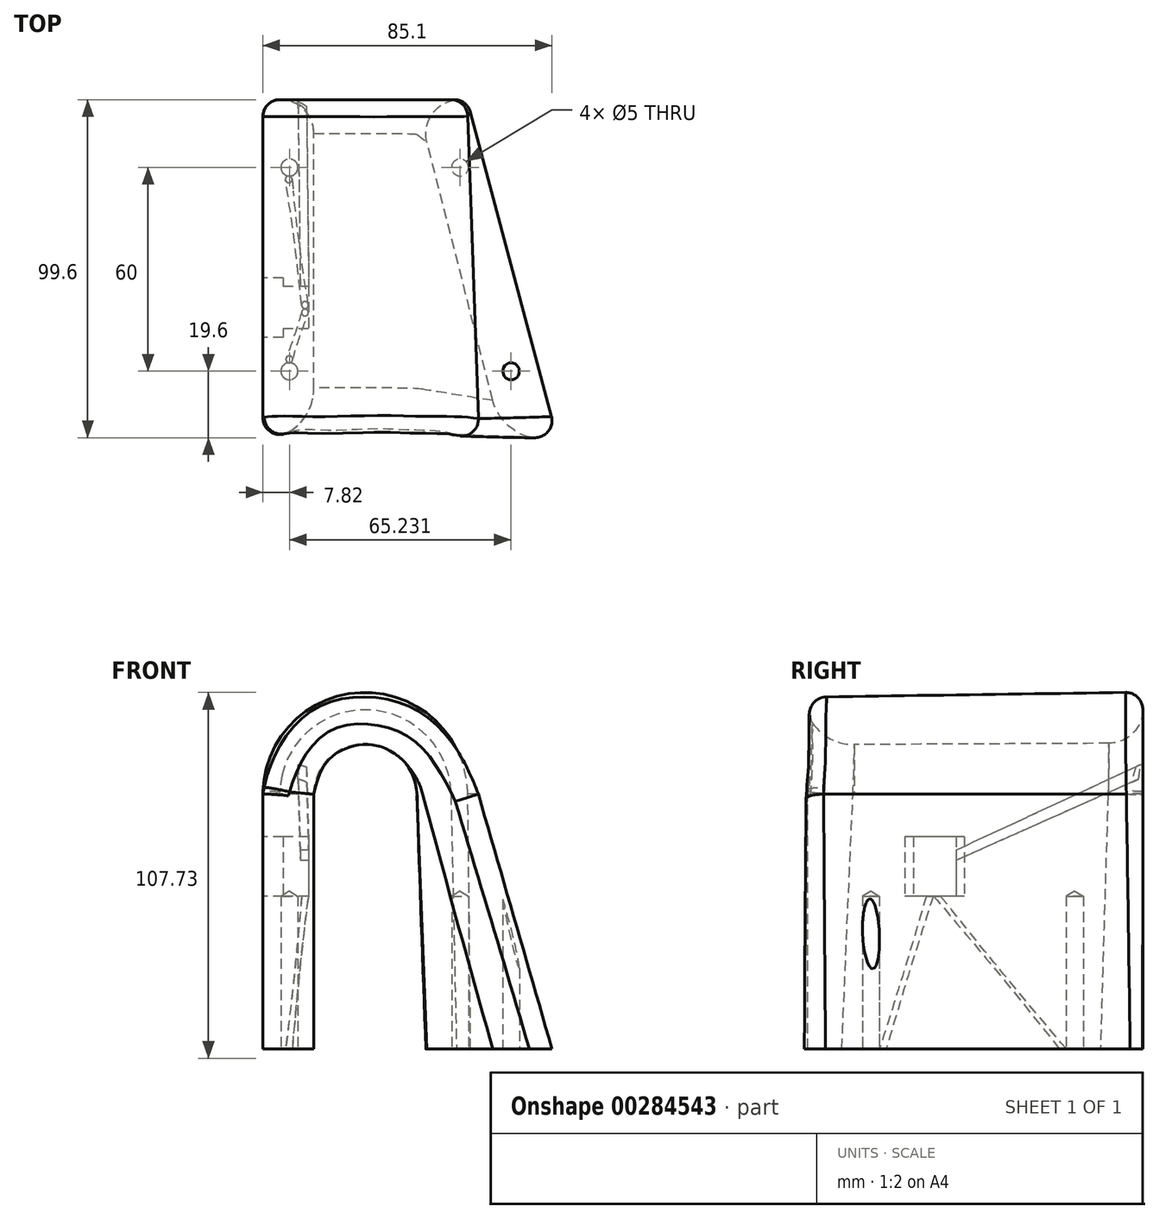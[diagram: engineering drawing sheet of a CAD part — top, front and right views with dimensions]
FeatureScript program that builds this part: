
annotation { "Feature Type Name" : "Feature", "Feature Type Description" : "" }
export const myFeature = defineFeature(function(context is Context, id is Id, definition is map)
    precondition{}
    {
        {
            var Q0;
            Q0=qCreatedBy(makeId("Top.planeOp"),FACE);
            var sketch = newSketch(context, id + "F0", { "sketchPlane" : qUnion([Q0])});
            skLineSegment(sketch, "E0.bottom", {"start": v(-34.5, 0) * mm, "end": v(-19.5, 0) * mm});
            skLineSegment(sketch, "E0.top", {"start": v(-34.5, 100) * mm, "end": v(-19.5, 100) * mm});
            skLineSegment(sketch, "E0.left", {"start": v(-34.5, 0) * mm, "end": v(-34.5, 100) * mm});
            skLineSegment(sketch, "E0.right", {"start": v(-19.5, 0) * mm, "end": v(-19.5, 100) * mm});
            skLineSegment(sketch, "E1", {"start": v(10.5, 100) * mm, "end": v(35.5, 0) * mm});
            skLineSegment(sketch, "E2", {"start": v(35.5, 0) * mm, "end": v(50.96, 0) * mm});
            skLineSegment(sketch, "E3", {"start": v(50.96, 0) * mm, "end": v(25.96, 100) * mm});
            skLineSegment(sketch, "E4", {"start": v(25.96, 100) * mm, "end": v(10.5, 100) * mm});
            skSolve(sketch);
        }
        {
            var Q0;
            Q0=qCreatedBy(makeId("Front.planeOp"),FACE);
            var sketch = newSketch(context, id + "F1", { "sketchPlane" : qUnion([Q0])});
            skLineSegment(sketch, "E5", {"start": v(-19.82, 0) * mm, "end": v(-19.82, 75) * mm});
            skLineSegment(sketch, "E6", {"start": v(-34.82, 0) * mm, "end": v(-34.82, 75) * mm});
            skLineSegment(sketch, "E7", {"start": v(12.65, 74.77) * mm, "end": v(35.77, 0) * mm});
            skLineSegment(sketch, "E8", {"start": v(28.84, 75) * mm, "end": v(51.88, 0) * mm});
            skFitSpline(sketch, "E9", {"points": [v(28.84, 75) * mm, v(10.53, 99.58) * mm, v(-18.34, 100.65) * mm, v(-34.82, 75) * mm], "startDerivative": vector(-36.75, 93.25) * mm, "endDerivative": vector(-17.89, -98.98) * mm});
            skFitSpline(sketch, "E10", {"points": [v(12.65, 74.77) * mm, v(0, 88.9) * mm, v(-14.2, 86.23) * mm, v(-19.82, 75) * mm], "startDerivative": vector(-14.46, 50.44) * mm, "endDerivative": vector(-10.98, -48.3) * mm});
            skLineSegment(sketch, "E11", {"start": v(51.88, 0) * mm, "end": v(35.77, 0) * mm});
            skLineSegment(sketch, "E12", {"start": v(-19.82, 0) * mm, "end": v(-34.82, 0) * mm});
            skSolve(sketch);
        }
        {
            var Q0;
            Q0=qCreatedBy(makeId("Front.planeOp"),FACE);
            cPlane(context, id + "F2", {"entities" : qUnion([Q0]), "cplaneType" : CPlaneType.OFFSET, "offset" : 100 * mm, "oppositeDirection" : true, "width" : 150 * mm, "height" : 150 * mm});
        }
        {
            var Q0;
            Q0=qCreatedBy(id+"F2.planeOp",FACE);
            var sketch = newSketch(context, id + "F3", { "sketchPlane" : qUnion([Q0])});
            skLineSegment(sketch, "E13", {"start": v(-34.82, 0) * mm, "end": v(-34.82, 75) * mm});
            skLineSegment(sketch, "E14", {"start": v(-19.82, 75) * mm, "end": v(-19.82, 0) * mm});
            skLineSegment(sketch, "E15", {"start": v(-19.82, 0) * mm, "end": v(-34.82, 0) * mm});
            skLineSegment(sketch, "E16", {"start": v(10.32, 0) * mm, "end": v(10.32, 75) * mm});
            skPoint(sketch, "E16.startSnap0", {"position": v(-27.32, 0) * mm});
            skLineSegment(sketch, "E17", {"start": v(10.32, 0) * mm, "end": v(25.32, 0) * mm});
            skLineSegment(sketch, "E18", {"start": v(25.32, 0) * mm, "end": v(25.32, 75) * mm});
            skArc(sketch, "E19", {"start": v(10.32, 75) * mm, "mid": v(-4.75, 90.07) * mm, "end": v(-19.82, 75) * mm});
            skArc(sketch, "E20", {"start": v(25.32, 75) * mm, "mid": v(-4.75, 105.07) * mm, "end": v(-34.82, 75) * mm});
            skSolve(sketch);
        }
        {
            var Q0;
            Q0 = qSketchRegion(id + "F1", true);
            var Q1;
            Q1 = qSketchRegion(id + "F3", true);
            loft(context, id + "F4", {"sheetProfilesArray" : [{ "sheetProfileEntities" : qUnion([Q0]) }, { "sheetProfileEntities" : qUnion([Q1]) }]});
        }
        {
            var Q0;
            Q0=makeQuery(id+"F4.opLoft","MID_CAP_EDGE",EDGE,{"disambiguationData":[OSD([sQuery(id+"F1.wireOp",EDGE,"E5"),sQuery(id+"F1.wireOp",EDGE,"E10"),sQuery(id+"F1.wireOp",EDGE,"E12")])],"capPos":0.0});
            var Q1;
            Q1=makeQuery(id+"F4.opLoft","MID_CAP_EDGE",EDGE,{"disambiguationData":[OSD([sQuery(id+"F1.wireOp",EDGE,"E5"),sQuery(id+"F1.wireOp",EDGE,"E7"),sQuery(id+"F1.wireOp",EDGE,"E10")])],"capPos":0.0});
            var Q2;
            Q2=makeQuery(id+"F4.opLoft","MID_CAP_EDGE",EDGE,{"disambiguationData":[OSD([sQuery(id+"F1.wireOp",EDGE,"E7"),sQuery(id+"F1.wireOp",EDGE,"E10"),sQuery(id+"F1.wireOp",EDGE,"E11")])],"capPos":0.0});
            fillet(context, id + "F5", {"entities" : qUnion([Q0, Q1, Q2]), "radius" : 15 * mm, "tangentPropagation" : true, "allowEdgeOverflow" : false});
        }
        {
            var Q0;
            Q0=makeQuery(id+"F4.opLoft","MID_CAP_EDGE",EDGE,{"disambiguationData":[OSD([sQuery(id+"F3.wireOp",EDGE,"E14"),sQuery(id+"F3.wireOp",EDGE,"E15"),sQuery(id+"F3.wireOp",EDGE,"E19")])],"capPos":1.0});
            var Q1;
            Q1=makeQuery(id+"F4.opLoft","MID_CAP_EDGE",EDGE,{"disambiguationData":[OSD([sQuery(id+"F3.wireOp",EDGE,"E14"),sQuery(id+"F3.wireOp",EDGE,"E16"),sQuery(id+"F3.wireOp",EDGE,"E19")])],"capPos":1.0});
            var Q2;
            Q2=makeQuery(id+"F4.opLoft","MID_CAP_EDGE",EDGE,{"disambiguationData":[OSD([sQuery(id+"F3.wireOp",EDGE,"E16"),sQuery(id+"F3.wireOp",EDGE,"E17"),sQuery(id+"F3.wireOp",EDGE,"E19")])],"capPos":1.0});
            fillet(context, id + "F6", {"entities" : qUnion([Q0, Q1, Q2]), "radius" : 10 * mm, "tangentPropagation" : true, "allowEdgeOverflow" : false});
        }
        {
            var Q0;
            Q0=makeQuery(id+"F0.imprint","IMPRINT",FACE,{"disambiguationData":[TD([[makeQuery(id+"F0.imprint","IMPRINT",EDGE,{"derivedFrom":sQuery(id+"F0.wireOp",EDGE,"E0.bottom")}),1.0]])]});
            var sketch = newSketch(context, id + "F7", { "sketchPlane" : qUnion([Q0])});
            skPoint(sketch, "E21", {"position": v(-27, 20) * mm});
            skPoint(sketch, "E22", {"position": v(-27, 80) * mm});
            skPoint(sketch, "E23", {"position": v(23.23, 80) * mm});
            skPoint(sketch, "E24", {"position": v(38.23, 20) * mm});
            skSolve(sketch);
        }
        {
            var Q0;
            Q0=sQuery(id+"F7.wireOp",VERTEX,"E21");
            var Q1;
            Q1=sQuery(id+"F7.wireOp",VERTEX,"E24");
            var Q2;
            Q2=sQuery(id+"F7.wireOp",VERTEX,"E23");
            var Q3;
            Q3=sQuery(id+"F7.wireOp",VERTEX,"E22");
            var Q4;
            Q4=makeQuery(id+"F4.opLoft","SWEPT_BODY",BODY,{"disambiguationData":[OSD([makeQuery(id+"F1.imprint","IMPRINT",FACE,{"disambiguationData":[TD([[makeQuery(id+"F1.imprint","IMPRINT",EDGE,{"derivedFrom":sQuery(id+"F1.wireOp",EDGE,"E5")}),1.0]])]}),makeQuery(id+"F3.imprint","IMPRINT",FACE,{"disambiguationData":[TD([[makeQuery(id+"F3.imprint","IMPRINT",EDGE,{"derivedFrom":sQuery(id+"F3.wireOp",EDGE,"E13")}),-1.0]])]})])]});
            hole(context, id + "F8", {"style" : HoleStyle.SIMPLE, "endStyle" : HoleEndStyle.BLIND, "oppositeDirection" : true, "holeDiameter" : 5 * mm, "holeDepth" : 45 * mm, "isTappedThrough" : true, "tappedDepth" : 12 * mm, "tapClearance" : 3, "locations" : qUnion([Q0, Q1, Q2, Q3]), "scope" : qUnion([Q4])});
        }
        {
            var Q0;
            Q0=makeQuery(id+"F4.opLoft","SWEPT_FACE",FACE,{"disambiguationData":[OSD([sQuery(id+"F1.wireOp",EDGE,"E6"),sQuery(id+"F1.wireOp",EDGE,"E9"),sQuery(id+"F1.wireOp",EDGE,"E12"),sQuery(id+"F3.wireOp",EDGE,"E13"),sQuery(id+"F3.wireOp",EDGE,"E15"),sQuery(id+"F3.wireOp",EDGE,"E20")])]});
            var sketch = newSketch(context, id + "F9", { "sketchPlane" : qUnion([Q0])});
            skLineSegment(sketch, "E25.bottom", {"start": v(-47.5, 62.5) * mm, "end": v(-30, 62.5) * mm});
            skLineSegment(sketch, "E25.top", {"start": v(-47.5, 45) * mm, "end": v(-30, 45) * mm});
            skLineSegment(sketch, "E25.left", {"start": v(-47.5, 62.5) * mm, "end": v(-47.5, 45) * mm});
            skLineSegment(sketch, "E25.right", {"start": v(-30, 62.5) * mm, "end": v(-30, 45) * mm});
            skSolve(sketch);
        }
        {
            var Q0;
            Q0=makeQuery(id+"F9.imprint","IMPRINT",FACE,{"disambiguationData":[TD([[makeQuery(id+"F9.imprint","IMPRINT",EDGE,{"derivedFrom":sQuery(id+"F9.wireOp",EDGE,"E25.bottom")}),-1.0]])]});
            extrude(context, id + "F10", {"entities" : qUnion([Q0]), "operationType" : NewBodyOperationType.REMOVE, "oppositeDirection" : true, "depth" : 6 * mm});
        }
        {
            var Q0;
            Q0=makeQuery(id+"F10.boolean.opBoolean","COPY",FACE,{"derivedFrom":makeQuery(id+"F10.opExtrude","CAP_FACE",FACE,{"disambiguationData":[OSD([sQuery(id+"F9.wireOp",EDGE,"E25.bottom"),sQuery(id+"F9.wireOp",EDGE,"E25.top"),sQuery(id+"F9.wireOp",EDGE,"E25.left"),sQuery(id+"F9.wireOp",EDGE,"E25.right")])],"isStart":false})});
            var sketch = newSketch(context, id + "F11", { "sketchPlane" : qUnion([Q0])});
            skLineSegment(sketch, "E26.bottom", {"start": v(-45, 62.5) * mm, "end": v(-32.5, 62.5) * mm});
            skLineSegment(sketch, "E26.top", {"start": v(-45, 45) * mm, "end": v(-32.5, 45) * mm});
            skLineSegment(sketch, "E26.left", {"start": v(-45, 62.5) * mm, "end": v(-45, 45) * mm});
            skLineSegment(sketch, "E26.right", {"start": v(-32.5, 62.5) * mm, "end": v(-32.5, 45) * mm});
            skSolve(sketch);
        }
        {
            var Q0;
            Q0=makeQuery(id+"F11.imprint","IMPRINT",FACE,{"disambiguationData":[TD([[makeQuery(id+"F11.imprint","IMPRINT",EDGE,{"derivedFrom":sQuery(id+"F11.wireOp",EDGE,"E26.bottom")}),-1.0]])]});
            extrude(context, id + "F12", {"entities" : qUnion([Q0]), "operationType" : NewBodyOperationType.REMOVE, "oppositeDirection" : true, "depth" : (13.5 - 6) * mm});
        }
        {
            var Q0;
            Q0=makeQuery(id+"F4.opLoft","MID_CAP_EDGE",EDGE,{"disambiguationData":[OSD([sQuery(id+"F3.wireOp",EDGE,"E13"),sQuery(id+"F3.wireOp",EDGE,"E15"),sQuery(id+"F3.wireOp",EDGE,"E20")])],"capPos":1.0});
            var Q1;
            Q1=makeQuery(id+"F4.opLoft","MID_CAP_EDGE",EDGE,{"disambiguationData":[OSD([sQuery(id+"F3.wireOp",EDGE,"E13"),sQuery(id+"F3.wireOp",EDGE,"E18"),sQuery(id+"F3.wireOp",EDGE,"E20")])],"capPos":1.0});
            fillet(context, id + "F13", {"entities" : qUnion([Q0, Q1]), "radius" : 5 * mm, "tangentPropagation" : true, "allowEdgeOverflow" : false});
        }
        {
            var Q0;
            {var subQ0=sQuery(id+"F1.wireOp",EDGE,"E12");Q0=makeQuery(id+"F5.opFillet","BLEND_EDGE",EDGE,{"blendedFrom":[makeQuery(id+"F4.opLoft","MID_CAP_EDGE",EDGE,{"disambiguationData":[OSD([sQuery(id+"F1.wireOp",EDGE,"E5"),sQuery(id+"F1.wireOp",EDGE,"E10"),subQ0])],"capPos":0.0}),makeQuery(id+"F4.opLoft","SWEPT_FACE",FACE,{"disambiguationData":[OSD([sQuery(id+"F1.wireOp",EDGE,"E6"),sQuery(id+"F1.wireOp",EDGE,"E9"),subQ0,sQuery(id+"F3.wireOp",EDGE,"E13"),sQuery(id+"F3.wireOp",EDGE,"E15"),sQuery(id+"F3.wireOp",EDGE,"E20")])]})],"blendedInto":[makeQuery(id+"F4.opLoft","SWEPT_FACE",FACE,{"disambiguationData":[OSD([sQuery(id+"F1.wireOp",EDGE,"E6"),sQuery(id+"F1.wireOp",EDGE,"E9"),subQ0,sQuery(id+"F3.wireOp",EDGE,"E13"),sQuery(id+"F3.wireOp",EDGE,"E15"),sQuery(id+"F3.wireOp",EDGE,"E20")])]})]});}
            var Q1;
            Q1=makeQuery(id+"F5.opFillet","BLEND_EDGE",EDGE,{"blendedFrom":[makeQuery(id+"F4.opLoft","MID_CAP_EDGE",EDGE,{"disambiguationData":[OSD([sQuery(id+"F1.wireOp",EDGE,"E5"),sQuery(id+"F1.wireOp",EDGE,"E7"),sQuery(id+"F1.wireOp",EDGE,"E10")])],"capPos":0.0}),makeQuery(id+"F4.opLoft","SWEPT_FACE",FACE,{"disambiguationData":[OSD([sQuery(id+"F1.wireOp",EDGE,"E6"),sQuery(id+"F1.wireOp",EDGE,"E8"),sQuery(id+"F1.wireOp",EDGE,"E9"),sQuery(id+"F3.wireOp",EDGE,"E13"),sQuery(id+"F3.wireOp",EDGE,"E18"),sQuery(id+"F3.wireOp",EDGE,"E20")])]})],"blendedInto":[makeQuery(id+"F4.opLoft","SWEPT_FACE",FACE,{"disambiguationData":[OSD([sQuery(id+"F1.wireOp",EDGE,"E6"),sQuery(id+"F1.wireOp",EDGE,"E8"),sQuery(id+"F1.wireOp",EDGE,"E9"),sQuery(id+"F3.wireOp",EDGE,"E13"),sQuery(id+"F3.wireOp",EDGE,"E18"),sQuery(id+"F3.wireOp",EDGE,"E20")])]})]});
            var Q2;
            Q2=makeQuery(id+"F4.opLoft","MID_CAP_EDGE",EDGE,{"disambiguationData":[OSD([sQuery(id+"F1.wireOp",EDGE,"E6"),sQuery(id+"F1.wireOp",EDGE,"E8"),sQuery(id+"F1.wireOp",EDGE,"E9")])],"capPos":0.0});
            var Q3;
            Q3=makeQuery(id+"F4.opLoft","MID_CAP_EDGE",EDGE,{"disambiguationData":[OSD([sQuery(id+"F1.wireOp",EDGE,"E8"),sQuery(id+"F1.wireOp",EDGE,"E9"),sQuery(id+"F1.wireOp",EDGE,"E11")])],"capPos":0.0});
            var Q4;
            Q4=makeQuery(id+"F5.opFillet","BLEND_EDGE",EDGE,{"blendedFrom":[makeQuery(id+"F4.opLoft","MID_CAP_EDGE",EDGE,{"disambiguationData":[OSD([sQuery(id+"F1.wireOp",EDGE,"E5"),sQuery(id+"F1.wireOp",EDGE,"E10"),sQuery(id+"F1.wireOp",EDGE,"E12")])],"capPos":0.0}),makeQuery(id+"F4.opLoft","SWEPT_FACE",FACE,{"disambiguationData":[OSD([sQuery(id+"F1.wireOp",EDGE,"E6"),sQuery(id+"F1.wireOp",EDGE,"E8"),sQuery(id+"F1.wireOp",EDGE,"E9"),sQuery(id+"F3.wireOp",EDGE,"E13"),sQuery(id+"F3.wireOp",EDGE,"E18"),sQuery(id+"F3.wireOp",EDGE,"E20")])]})],"blendedInto":[makeQuery(id+"F4.opLoft","SWEPT_FACE",FACE,{"disambiguationData":[OSD([sQuery(id+"F1.wireOp",EDGE,"E6"),sQuery(id+"F1.wireOp",EDGE,"E8"),sQuery(id+"F1.wireOp",EDGE,"E9"),sQuery(id+"F3.wireOp",EDGE,"E13"),sQuery(id+"F3.wireOp",EDGE,"E18"),sQuery(id+"F3.wireOp",EDGE,"E20")])]})]});
            fillet(context, id + "F14", {"entities" : qUnion([Q0, Q1, Q2, Q3, Q4]), "radius" : 5 * mm, "tangentPropagation" : true, "allowEdgeOverflow" : false});
        }
        {
            var Q0;
            Q0=makeQuery(id+"F0.imprint","IMPRINT",FACE,{"disambiguationData":[TD([[makeQuery(id+"F0.imprint","IMPRINT",EDGE,{"derivedFrom":sQuery(id+"F0.wireOp",EDGE,"E0.bottom")}),1.0]])]});
            var sketch = newSketch(context, id + "F15", { "sketchPlane" : qUnion([Q0])});
            skPoint(sketch, "E27", {"position": v(-27.05, 23.5) * mm});
            skPoint(sketch, "E28", {"position": v(-27.2, 76.5) * mm});
            skCircle(sketch, "E29", {"center": v(-27.05, 23.5) * mm, "radius": 1 * mm});
            skCircle(sketch, "E30", {"center": v(-27.2, 76.5) * mm, "radius": 1 * mm});
            skSolve(sketch);
        }
        {
            var Q0;
            Q0=makeQuery(id+"F12.boolean.opBoolean","MERGE",FACE,{"derivedFrom":[makeQuery(id+"F10.boolean.opBoolean","COPY",FACE,{"derivedFrom":makeQuery(id+"F10.opExtrude","SWEPT_FACE",FACE,{"disambiguationData":[OSD([sQuery(id+"F9.wireOp",EDGE,"E25.top")])]})}),makeQuery(id+"F12.opExtrude","SWEPT_FACE",FACE,{"disambiguationData":[OSD([sQuery(id+"F11.wireOp",EDGE,"E26.top")])]})]});
            var sketch = newSketch(context, id + "F16", { "sketchPlane" : qUnion([Q0])});
            skPoint(sketch, "E31", {"position": v(-22.42, 37.28) * mm});
            skPoint(sketch, "E32", {"position": v(-22.42, 39.48) * mm});
            skCircle(sketch, "E33", {"center": v(-22.42, 37.28) * mm, "radius": 1 * mm});
            skCircle(sketch, "E34", {"center": v(-22.42, 39.48) * mm, "radius": 1 * mm});
            skSolve(sketch);
        }
        {
            var Q0;
            Q0=makeQuery(id+"F16.imprint","IMPRINT",FACE,{"disambiguationData":[TD([[makeQuery(id+"F16.imprint","IMPRINT",EDGE,{"derivedFrom":sQuery(id+"F16.wireOp",EDGE,"E33")}),1.0]])]});
            var Q1;
            Q1=makeQuery(id+"F15.imprint","IMPRINT",FACE,{"disambiguationData":[TD([[makeQuery(id+"F15.imprint","IMPRINT",EDGE,{"derivedFrom":sQuery(id+"F15.wireOp",EDGE,"E29")}),1.0]])]});
            loft(context, id + "F17", {"operationType" : NewBodyOperationType.REMOVE, "sheetProfilesArray" : [{ "sheetProfileEntities" : qUnion([Q0]) }, { "sheetProfileEntities" : qUnion([Q1]) }]});
        }
        {
            var Q1;
            Q1=makeQuery(id+"F15.imprint","IMPRINT",FACE,{"disambiguationData":[TD([[makeQuery(id+"F15.imprint","IMPRINT",EDGE,{"derivedFrom":sQuery(id+"F15.wireOp",EDGE,"E30")}),1.0]])]});
            var Q2;
            Q2=makeQuery(id+"F16.imprint","IMPRINT",FACE,{"disambiguationData":[TD([[makeQuery(id+"F16.imprint","IMPRINT",EDGE,{"derivedFrom":sQuery(id+"F16.wireOp",EDGE,"E34")}),1.0]])]});
            loft(context, id + "F18", {"operationType" : NewBodyOperationType.REMOVE, "sheetProfilesArray" : [{ "sheetProfileEntities" : qUnion([Q1]) }, { "sheetProfileEntities" : qUnion([Q2]) }]});
        }
        {
            var Q0;
            Q0=makeQuery(id+"F12.boolean.opBoolean","COPY",FACE,{"derivedFrom":makeQuery(id+"F12.opExtrude","SWEPT_FACE",FACE,{"disambiguationData":[OSD([sQuery(id+"F11.wireOp",EDGE,"E26.left")])]})});
            var sketch = newSketch(context, id + "F19", { "sketchPlane" : qUnion([Q0])});
            skLineSegment(sketch, "E35.bottom", {"start": v(-21.32, 58.5) * mm, "end": v(-23.82, 58.5) * mm});
            skLineSegment(sketch, "E35.top", {"start": v(-21.32, 55.5) * mm, "end": v(-23.82, 55.5) * mm});
            skLineSegment(sketch, "E35.left", {"start": v(-21.32, 58.5) * mm, "end": v(-21.32, 55.5) * mm});
            skLineSegment(sketch, "E35.right", {"start": v(-23.82, 58.5) * mm, "end": v(-23.82, 55.5) * mm});
            skSolve(sketch);
        }
        {
            var Q0;
            Q0=qCreatedBy(id+"F2.planeOp",FACE);
            var sketch = newSketch(context, id + "F20", { "sketchPlane" : qUnion([Q0])});
            skLineSegment(sketch, "E36.bottom", {"start": v(-24.5, 84) * mm, "end": v(-22, 84) * mm});
            skLineSegment(sketch, "E36.top", {"start": v(-24.5, 80) * mm, "end": v(-22, 80) * mm});
            skLineSegment(sketch, "E36.left", {"start": v(-24.5, 84) * mm, "end": v(-24.5, 80) * mm});
            skLineSegment(sketch, "E36.right", {"start": v(-22, 84) * mm, "end": v(-22, 80) * mm});
            skSolve(sketch);
        }
        {
            var Q1;
            Q1=makeQuery(id+"F20.imprint","IMPRINT",FACE,{"disambiguationData":[TD([[makeQuery(id+"F20.imprint","IMPRINT",EDGE,{"derivedFrom":sQuery(id+"F20.wireOp",EDGE,"E36.bottom")}),-1.0]])]});
            var Q2;
            Q2=makeQuery(id+"F19.imprint","IMPRINT",FACE,{"disambiguationData":[TD([[makeQuery(id+"F19.imprint","IMPRINT",EDGE,{"derivedFrom":sQuery(id+"F19.wireOp",EDGE,"E35.bottom")}),1.0]])]});
            loft(context, id + "F21", {"operationType" : NewBodyOperationType.REMOVE, "sheetProfilesArray" : [{ "sheetProfileEntities" : qUnion([Q1]) }, { "sheetProfileEntities" : qUnion([Q2]) }]});
        }
    });
